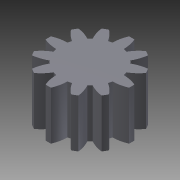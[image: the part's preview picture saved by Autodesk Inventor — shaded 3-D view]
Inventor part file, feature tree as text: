
AUTODESK INVENTOR PART (.ipt)
format: ipt  version: 2011 (Build 150239000, 239)  size: 150,528 bytes
history: native  units: mm (DEFAULTED — no unit token found)
features: plane x3, extrude x2, other x2, sketch x2
ambient origin geometry x8: Origin, YZ Plane, XZ Plane, XY Plane, X Axis, Y Axis, Z Axis, Center Point
bodies: Solid1 (feature_tree)
feature tree (9):
  extrude  "Extrusion1"  Depth=12.75mm TaperAngle=0.0deg
  plane  "Work Plane2"
  plane  "Work Plane8"
  plane  "Work Plane9"
  other  "Spur Gear"
  sketch  "Sketch1"  dims[d0=22.0mm d1=12.75mm d2=0.0mm]
  sketch  "Sketch2"  dims[d3=19.05mm d4=10.0mm d5=0.0mm d16=19.05mm d17=0.0mm d34=15.0deg d39=0.0mm d41=0.0mm d43=19.05mm d46=19.05mm d47=0.0mm d48=0.0mm]
  other  "Srf1"
  extrude  "ExtrusionSrf1"  Depth=10.0mm TaperAngle=0.0deg
